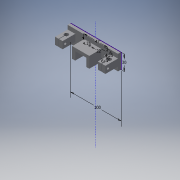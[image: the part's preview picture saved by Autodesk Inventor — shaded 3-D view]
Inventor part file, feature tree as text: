
AUTODESK INVENTOR PART (.ipt)
format: ipt  version: 2019 (Build 230136000, 136)  size: 199,168 bytes
history: native  units: in
note: dims shown in document units (in); Inventor stores cm internally (conversion verified against a paired STEP export)
features: extrude x7, sketch x6
ambient origin geometry x8: Origin, YZ Plane, XZ Plane, XY Plane, X Axis, Y Axis, Z Axis, Center Point
bodies: Solid1 (feature_tree)
feature tree (13):
  sketch  "Sketch1"  dims[d1=1.1811in d2=3.937in]
  extrude  "Extrusion1"  Depth=3.937in
  extrude  "Extrusion2"  Depth=0.2362in
  extrude  "Extrusion3"  Depth=0.2362in
  extrude  "Extrusion4"  Depth=1.1811in TaperAngle=0.0deg
  extrude  "Extrusion5"  Depth=0.1673in
  extrude  "Extrusion6"  Depth=0.3937in
  extrude  "Extrusion7"  Depth=1.1811in TaperAngle=0.0deg
  sketch  "Sketch2"  dims[d3=0.8661in d4=0.2362in]
  sketch  "Sketch3"  dims[d5=0.6299in d6=0.2362in]
  sketch  "Sketch4"  dims[d7=0.2362in d8=0.0in d9=1.1811in d10=0.0in]
  sketch  "Sketch5"  dims[d11=0.1673in d13=0.1673in]
  sketch  "Sketch6"  dims[d14=0.1673in d15=0.4724in d16=1.1811in d17=0.0in d18=1.8504in d19=0.5906in d20=0.5512in d21=0.9843in d22=0.0in d23=0.315in d24=0.6299in d25=0.0394in d26=0.315in d27=0.0394in d28=1.1811in d29=0.0in d30=0.1673in d32=1.1811in d33=0.0in d34=0.3937in d35=0.0in]
